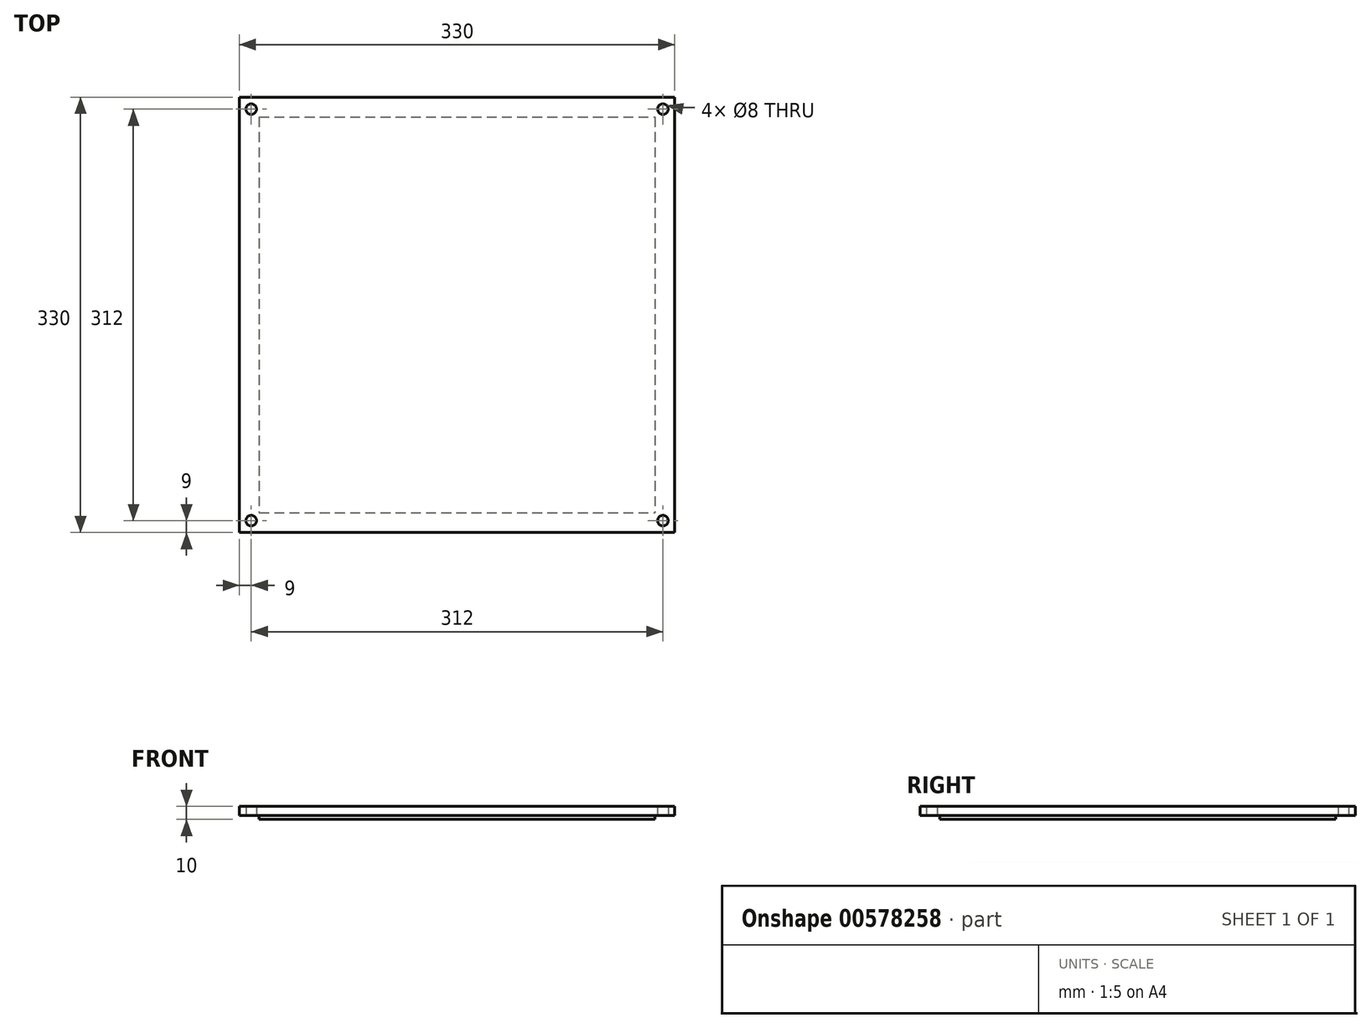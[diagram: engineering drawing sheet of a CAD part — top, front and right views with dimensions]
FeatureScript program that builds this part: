
annotation { "Feature Type Name" : "Feature", "Feature Type Description" : "" }
export const myFeature = defineFeature(function(context is Context, id is Id, definition is map)
    precondition{}
    {
        {
            var Q0;
            Q0=qCreatedBy(makeId("Top.planeOp"),FACE);
            var sketch = newSketch(context, id + "F0", { "sketchPlane" : qUnion([Q0])});
            skLineSegment(sketch, "E0.bottom", {"start": v(-150, 150) * mm, "end": v(150, 150) * mm});
            skLineSegment(sketch, "E0.top", {"start": v(-150, -150) * mm, "end": v(150, -150) * mm});
            skLineSegment(sketch, "E0.left", {"start": v(-150, 150) * mm, "end": v(-150, -150) * mm});
            skLineSegment(sketch, "E0.right", {"start": v(150, 150) * mm, "end": v(150, -150) * mm});
            skPoint(sketch, "E0.middle", {"position": v(0, 0) * mm});
            skLineSegment(sketch, "E1.left", {"start": v(-150, 150) * mm, "end": v(-150, 150) * mm});
            skLineSegment(sketch, "E1.right", {"start": v(150, 150) * mm, "end": v(150, 150) * mm});
            skLineSegment(sketch, "E2.bottom", {"start": v(-165, 165) * mm, "end": v(165, 165) * mm});
            skLineSegment(sketch, "E2.top", {"start": v(-165, -165) * mm, "end": v(165, -165) * mm});
            skLineSegment(sketch, "E2.left", {"start": v(-165, 165) * mm, "end": v(-165, -165) * mm});
            skLineSegment(sketch, "E2.right", {"start": v(165, 165) * mm, "end": v(165, -165) * mm});
            skSolve(sketch);
        }
        {
            var Q0;
            Q0=makeQuery(id+"F0.imprint","IMPRINT",FACE,{"disambiguationData":[TD([[makeQuery(id+"F0.imprint","IMPRINT",EDGE,{"derivedFrom":sQuery(id+"F0.wireOp",EDGE,"E0.top")}),-1.0]])]});
            var Q1;
            Q1=makeQuery(id+"F0.imprint","IMPRINT",FACE,{"disambiguationData":[TD([[makeQuery(id+"F0.imprint","IMPRINT",EDGE,{"derivedFrom":sQuery(id+"F0.wireOp",EDGE,"E0.top")}),1.0]])]});
            extrude(context, id + "F1", {"entities" : qUnion([Q0, Q1]), "depth" : 7 * mm, "offsetDistance" : 25 * mm});
        }
        {
            var Q0;
            Q0=makeQuery(id+"F0.imprint","IMPRINT",FACE,{"disambiguationData":[TD([[makeQuery(id+"F0.imprint","IMPRINT",EDGE,{"derivedFrom":sQuery(id+"F0.wireOp",EDGE,"E0.top")}),1.0]])]});
            extrude(context, id + "F2", {"entities" : qUnion([Q0]), "operationType" : NewBodyOperationType.ADD, "oppositeDirection" : true, "depth" : 3 * mm, "offsetDistance" : 25 * mm});
        }
        {
            var Q0;
            Q0=qCreatedBy(makeId("Top.planeOp"),FACE);
            var sketch = newSketch(context, id + "F3", { "sketchPlane" : qUnion([Q0])});
            skCircle(sketch, "E3", {"center": v(-156, 156) * mm, "radius": 4 * mm});
            skCircle(sketch, "E4.MirrorC", {"center": v(156, 156) * mm, "radius": 4 * mm});
            skCircle(sketch, "E5.MirrorC", {"center": v(156, -156) * mm, "radius": 4 * mm});
            skCircle(sketch, "E6.MirrorC", {"center": v(-156, -156) * mm, "radius": 4 * mm});
            skSolve(sketch);
        }
        {
            var Q0;
            Q0=qSketchRegion(id+"F3",true);
            extrude(context, id + "F4", {"entities" : qUnion([Q0]), "operationType" : NewBodyOperationType.REMOVE, "depth" : 8 * mm, "offsetDistance" : 25 * mm});
        }
    });
